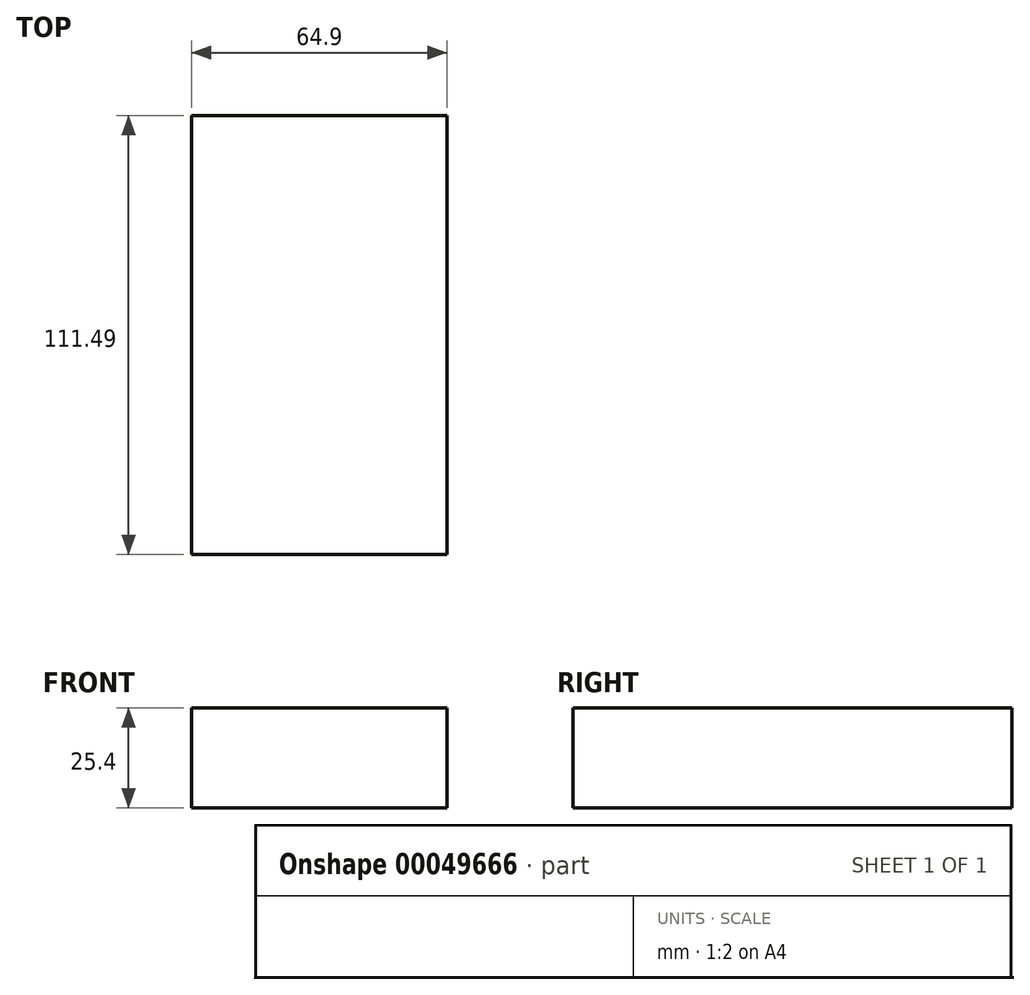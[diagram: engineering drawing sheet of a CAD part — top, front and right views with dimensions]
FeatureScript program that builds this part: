
annotation { "Feature Type Name" : "Feature", "Feature Type Description" : "" }
export const myFeature = defineFeature(function(context is Context, id is Id, definition is map)
    precondition{}
    {
        {
            var Q0;
            Q0=qCreatedBy(makeId("Top.planeOp"),FACE);
            var sketch = newSketch(context, id + "F0", { "sketchPlane" : qUnion([Q0])});
            skLineSegment(sketch, "E0.bottom", {"start": v(-134.22, 71.3) * mm, "end": v(-69.32, 71.3) * mm});
            skLineSegment(sketch, "E0.top", {"start": v(-134.22, -40.2) * mm, "end": v(-69.32, -40.2) * mm});
            skLineSegment(sketch, "E0.left", {"start": v(-134.22, 71.3) * mm, "end": v(-134.22, -40.2) * mm});
            skLineSegment(sketch, "E0.right", {"start": v(-69.32, 71.3) * mm, "end": v(-69.32, -40.2) * mm});
            skSolve(sketch);
        }
        {
            var Q0;
            Q0=makeQuery(id+"F0.imprint","IMPRINT",FACE,{"disambiguationData":[TD([[makeQuery(id+"F0.imprint","IMPRINT",EDGE,{"derivedFrom":sQuery(id+"F0.wireOp",EDGE,"E0.bottom")}),-1.0]])]});
            extrude(context, id + "F1", {"entities" : qUnion([Q0]), "depth" : 25.4 * mm});
        }
    });
